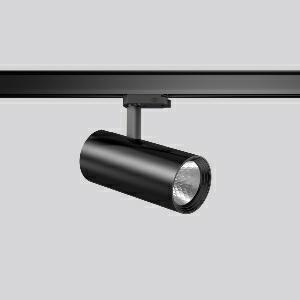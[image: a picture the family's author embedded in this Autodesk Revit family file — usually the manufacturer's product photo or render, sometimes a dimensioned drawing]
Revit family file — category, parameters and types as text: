
# Revit family: deecos_s_mini_742204_003_1_76_c19b
name_source: partatom
category: Lighting Fixtures
units: mm (PartAtom-declared; Revit-internal decimal feet)

## family parameters
Cut with Voids When Loaded = No
Host = Face
Light Source = No
Part Type = Normal
Room Calculation Point = No
Round Connector Dimension = Use Diameter
Shared = No

## types (1)
- DEECOS S mini (1 x LED Modul 940, 3700 lm, 4000)
    Apparent Load = 29 VA
    Approval mark = CE
    CIE Flux Codes = 99 100 100 100 100
    Color Rendering = 92
    Color Temperature = 4000
    Default Elevation = 1800 mm
    Description = Series: DEECOS S mini
LED surface-mounted projector in modern design with no visible cooling ribs. Housing: die-cast aluminium, powder-coated. Rotation range: 356°. Swivel range: 90°. Black plastic ring and recessed LED to prevent glare from the side. Optical assembly with reflector made of MIRO-Silver with 98% total light reflection for outstanding efficiency - can be changed without tools. Best colour rendering index Ra>90. With adapter for RZB 3-circuit DALI tracks. Suitable for Track on ceiling, Wall track. High quality converter without flickering and stroboscopic effect. The following accessories can be mounted without use of tools: interchangeable lenses, decorative glasses, honeycomb louvre, clear and frosted diffusers, white interchangeable plastic ring. 
Colour: deep black, matt (RAL 9005)
Diameter: 87 mm
Height: 214 mm
Lamp: LED
Socket: without socket
Colour temperature: 4000K
Colour rendering index (CRI): 92
System power: 29 W
Rated luminous flux: 3700 lm
Luminous efficiency: 128 lm/W
Control gear: Converter, dimmable, DALI
Protection class: I
Type of protection: IP 20
    Height = 214 mm
    Lamp = 1 x LED Modul 940
    Lamp Light Flux = 3700 lm
    Lamp count = 1
    Length = 87 mm
    Lifetime = 50000 h
    Luminous efficacy = 128 lm/W
    Manufacturer = RZB
    ModVariant = No
    Model = 742204.003.1.76
    Mounting Place = Ceiling
    Mounting Type = Rail mounted
    Number of Poles = 1
    OnlyDefault = Yes
    Power Factor = 1
    Product Name = DEECOS S mini
    Product group = Track mounted projectors
    ProductGroupID = 301
    Protection Class = Protection class I
    Protection Degree = IP 20
    RLX_Detail_Level = 1
    RLX_Emergency_Light_Flux = 0 lm
    RLX_Emergency_Type = 0
    RLX_Emergency_Type_DB = No
    RlxData = <blob elided: 38805 chars, md5=7352c4f2>
    Socket = socket
    Standby Power = 0 W
    System Light Flux = 3700 lm
    System Power = 29 W
    Type Comments = Product without accessories
    Type Image = 741926.003.jpg
    URL = http://relux.com
    VarID = ---
    Voltage = 230 V
    Voltage Range = 220-240 V
    Weight = 0.00 kg
    Width = 0 mm  [stored 0 ft]

note: [stored X ft] marks values corroborated as IEEE doubles in the binary element streams (Revit-internal decimal feet)

## geometry (parser evidence)
native form markers: Blend x4, Sweep x11
no freeform markers — native parametric forms only
